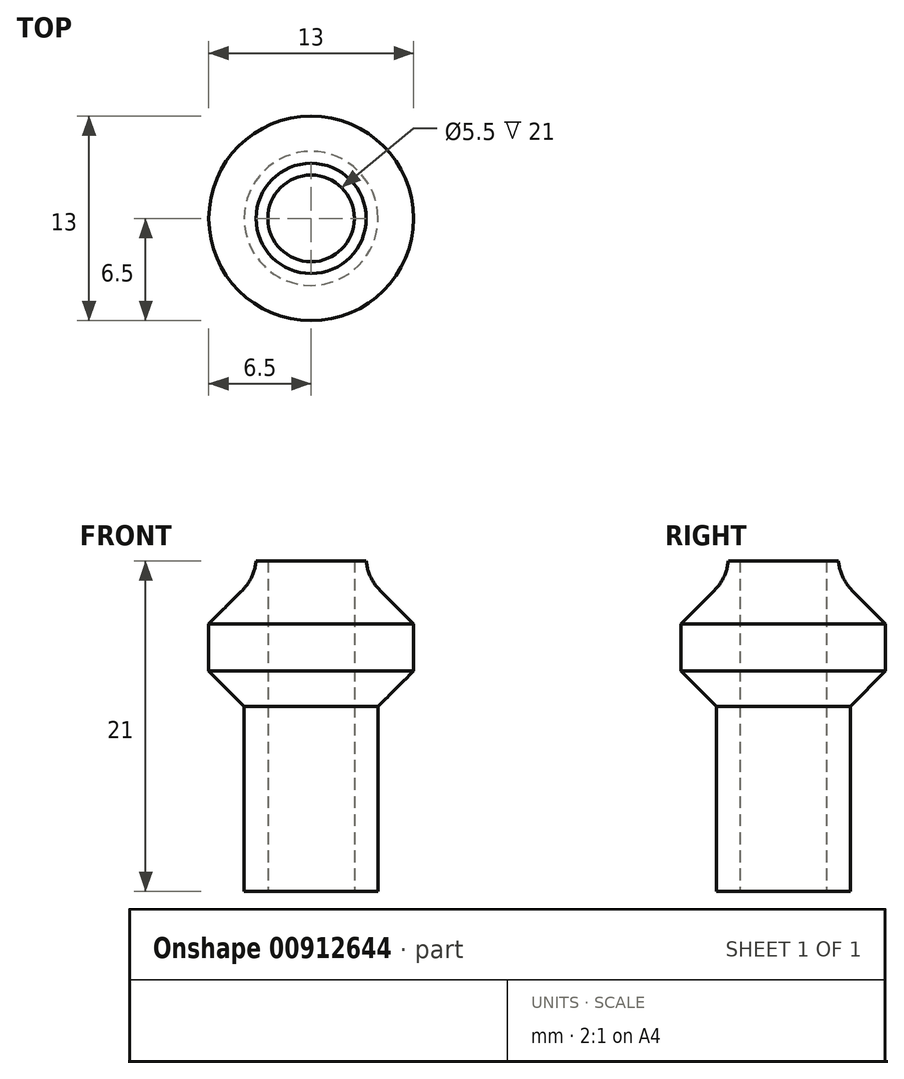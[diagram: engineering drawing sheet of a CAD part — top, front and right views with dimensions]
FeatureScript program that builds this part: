
annotation { "Feature Type Name" : "Feature", "Feature Type Description" : "" }
export const myFeature = defineFeature(function(context is Context, id is Id, definition is map)
    precondition{}
    {
        {
            var Q0;
            Q0=qCreatedBy(makeId("Top.planeOp"),FACE);
            var sketch = newSketch(context, id + "F0", { "sketchPlane" : qUnion([Q0])});
            skCircle(sketch, "E0", {"center": v(0, 0) * mm, "radius": 2.75 * mm});
            skCircle(sketch, "E1", {"center": v(0, 0) * mm, "radius": 4.25 * mm});
            skSolve(sketch);
        }
        {
            var Q0;
            Q0=makeQuery(id+"F0.imprint","IMPRINT",FACE,{"disambiguationData":[TD([[makeQuery(id+"F0.imprint","IMPRINT",EDGE,{"derivedFrom":sQuery(id+"F0.wireOp",EDGE,"E0")}),-1.0]])]});
            extrude(context, id + "F1", {"entities" : qUnion([Q0]), "depth" : 10 * mm, "offsetDistance" : 25 * mm});
        }
        {
            var Q0;
            Q0=makeQuery(id+"F1.opExtrude","CAP_FACE",FACE,{"disambiguationData":[OSD([sQuery(id+"F0.wireOp",EDGE,"E0"),sQuery(id+"F0.wireOp",EDGE,"E1")])],"isStart":false});
            var sketch = newSketch(context, id + "F2", { "sketchPlane" : qUnion([Q0])});
            skCircle(sketch, "E2", {"center": v(0, 0) * mm, "radius": 6.5 * mm});
            skSolve(sketch);
        }
        {
            var Q0;
            Q0=makeQuery(id+"F2.imprint","IMPRINT",FACE,{"disambiguationData":[TD([[makeQuery(id+"F2.imprint","IMPRINT",EDGE,{"derivedFrom":sQuery(id+"F2.wireOp",EDGE,"E2")}),1.0]])]});
            var Q1;
            Q1=makeQuery(id+"F2.imprint","IMPRINT",FACE,{"disambiguationData":[TD([[makeQuery(id+"F2.imprint","IMPRINT",EDGE,{"derivedFrom":makeQuery(id+"F1.opExtrude","CAP_EDGE",EDGE,{"disambiguationData":[OSD([sQuery(id+"F0.wireOp",EDGE,"E0")])],"isStart":false})}),-1.0]])]});
            extrude(context, id + "F3", {"entities" : qUnion([Q0, Q1]), "operationType" : NewBodyOperationType.ADD, "depth" : 10 * mm, "offsetDistance" : 25 * mm});
        }
        {
            var Q0;
            Q0=makeQuery(id+"F3.opExtrude","CAP_FACE",FACE,{"disambiguationData":[OSD([sQuery(id+"F0.wireOp",EDGE,"E0"),sQuery(id+"F2.wireOp",EDGE,"E2")])],"isStart":false});
            var sketch = newSketch(context, id + "F4", { "sketchPlane" : qUnion([Q0])});
            skCircle(sketch, "E3", {"center": v(0, 0) * mm, "radius": 3.5 * mm});
            skSolve(sketch);
        }
        {
            var Q0;
            Q0=makeQuery(id+"F4.imprint","IMPRINT",FACE,{"disambiguationData":[TD([[makeQuery(id+"F4.imprint","IMPRINT",EDGE,{"derivedFrom":sQuery(id+"F4.wireOp",EDGE,"E3")}),1.0]])]});
            extrude(context, id + "F5", {"entities" : qUnion([Q0]), "operationType" : NewBodyOperationType.ADD, "depth" : 1 * mm, "offsetDistance" : 25 * mm});
        }
        {
            var Q0;
            Q0=makeQuery(id+"F3.opExtrude","CAP_EDGE",EDGE,{"disambiguationData":[OSD([sQuery(id+"F2.wireOp",EDGE,"E2")])],"isStart":false});
            chamfer(context, id + "F6", {"entities" : qUnion([Q0]), "width" : 3 * mm, "tangentPropagation" : true});
        }
        {
            var Q0;
            Q0=makeQuery(id+"F6.opChamfer","BLEND_EDGE",EDGE,{"blendedFrom":[makeQuery(id+"F3.opExtrude","CAP_EDGE",EDGE,{"disambiguationData":[OSD([sQuery(id+"F2.wireOp",EDGE,"E2")])],"isStart":false}),makeQuery(id+"F5.opExtrude","SWEPT_FACE",FACE,{"disambiguationData":[OSD([sQuery(id+"F4.wireOp",EDGE,"E3")])]})],"blendedInto":[makeQuery(id+"F5.opExtrude","SWEPT_FACE",FACE,{"disambiguationData":[OSD([sQuery(id+"F4.wireOp",EDGE,"E3")])]})]});
            fillet(context, id + "F7", {"entities" : qUnion([Q0]), "radius" : 3 * mm, "tangentPropagation" : true, "allowEdgeOverflow" : false});
        }
        {
            var Q0;
            Q0=makeQuery(id+"F3.opExtrude","CAP_EDGE",EDGE,{"disambiguationData":[OSD([sQuery(id+"F2.wireOp",EDGE,"E2")])],"isStart":true});
            chamfer(context, id + "F8", {"entities" : qUnion([Q0]), "width" : 4 * mm, "tangentPropagation" : true});
        }
    });
